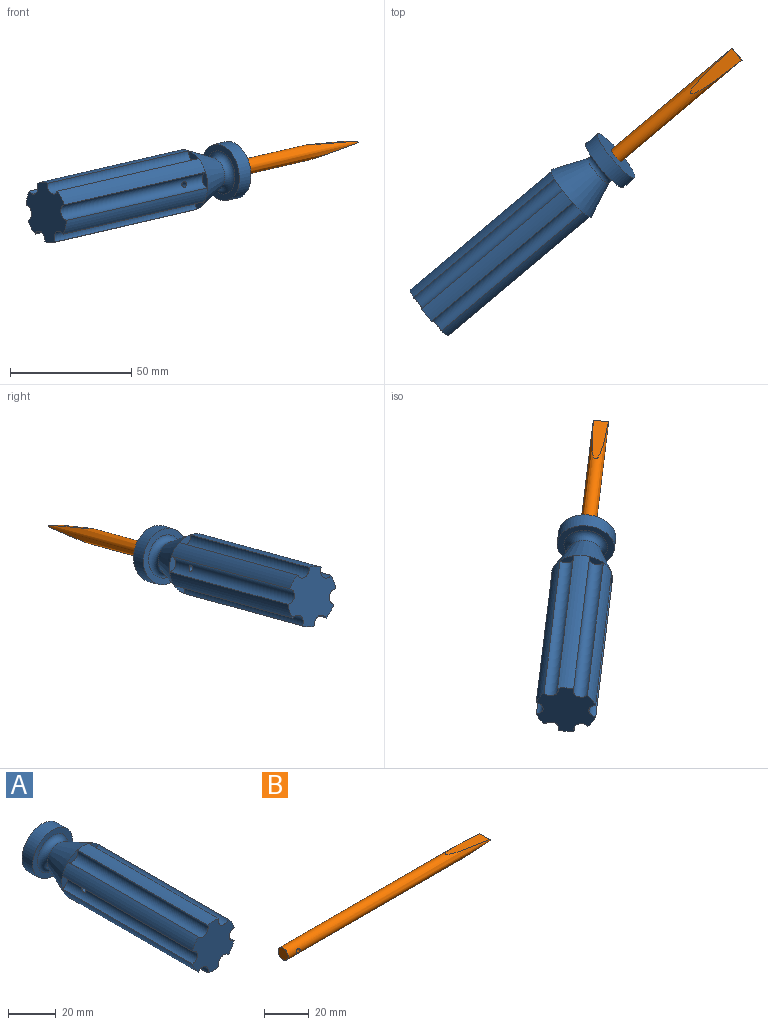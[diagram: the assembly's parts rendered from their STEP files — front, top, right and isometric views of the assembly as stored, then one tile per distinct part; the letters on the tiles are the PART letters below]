
ASSEMBLY  parts=2 mates=1
PART A: 28 faces, bbox 25.4x101.6x25.4 mm
  f0: cylinder r=12.7mm len=77.22mm, axis (0,-1,0), area 516.8mm2, adj f5,f6,f21,f23
  f1: cylinder r=12.7mm len=77.22mm, axis (0,-1,0), area 516.8mm2, adj f5,f6,f19,f21
  f2: cylinder r=12.7mm len=77.22mm, axis (0,-1,0), area 516.8mm2, adj f5,f6,f17,f19
  f3: cylinder r=12.7mm len=77.22mm, axis (0,-1,0), area 516.8mm2, adj f5,f6,f15,f17
  f4: cylinder r=12.7mm len=77.22mm, axis (0,-1,0), area 516.8mm2, adj f5,f6,f13,f15
  f5: plane 25.4x24.55mm, normal (0,-1,0), area 411.9mm2, adj f0,f1,f2,f3,f4,f7,f13,f15
  f6: cone r=12.7mm half-angle=22.3deg, axis (0,-1,0), area 959.6mm2, adj f0,f1,f2,f3,f4,f7,f11,f12
  f7: cylinder r=12.7mm len=77.22mm, axis (0,-1,0), area 516.8mm2, adj f5,f6,f13,f23
  f8: plane 23.71x23.71mm, normal (0,1,0), area 409.9mm2, adj f9,f24
  f9: cylinder r=11.86mm len=23.71mm, axis (0,-1,0), area 473mm2, adj f8,f10
  f10: plane 23.71x23.71mm, normal (0,-1,0), area 183.5mm2, adj f9,f11
  f11: torus R=9.06mm, axis (0,-1,0), area 226.9mm2, adj f6,f10
  f12: plane 6.53x3.25mm, normal (0,-1,0), area 15.8mm2, adj f6,f13
  f13: cylinder r=3.3mm len=77.22mm, axis (0,-1,0), area 721.4mm2, adj f4,f5,f7,f12,f26
  f14: plane 5.89x4.52mm, normal (0,-1,0), area 15.8mm2, adj f6,f15
  f15: cylinder r=3.3mm len=77.22mm, axis (0,-1,0), area 726mm2, adj f3,f4,f5,f14
  f16: plane 5.89x4.52mm, normal (0,-1,0), area 15.8mm2, adj f6,f17
  f17: cylinder r=3.3mm len=77.22mm, axis (0,-1,0), area 726mm2, adj f2,f3,f5,f16
  f18: plane 6.53x3.25mm, normal (0,-1,0), area 15.8mm2, adj f6,f19
  f19: cylinder r=3.3mm len=77.22mm, axis (0,-1,0), area 721.4mm2, adj f1,f2,f5,f18,f27
  f20: plane 5.89x4.52mm, normal (0,-1,0), area 15.8mm2, adj f6,f21
  f21: cylinder r=3.3mm len=77.22mm, axis (0,-1,0), area 726mm2, adj f0,f1,f5,f20
  f22: plane 5.89x4.52mm, normal (0,-1,0), area 15.8mm2, adj f6,f23
  f23: cylinder r=3.3mm len=77.22mm, axis (0,-1,0), area 726mm2, adj f0,f5,f7,f22
  f24: cylinder r=3.17mm len=60.96mm, axis (0,-1,0), area 1207mm2, adj f8,f25,f26,f27
  f25: plane 6.35x6.35mm, normal (0,1,0), area 31.7mm2, adj f24
  f26: cylinder r=1.19mm len=6.74mm, axis (1,0,0), area 48.8mm2, adj f13,f24
  f27: cylinder r=1.19mm len=6.74mm, axis (1,0,0), area 48.8mm2, adj f19,f24
PART B: 6 faces, bbox 127x6.4x6.4 mm
  f0: cylinder r=3.17mm len=127mm, axis (1,0,0), area 2230.3mm2, adj f1,f2,f3,f4,f5
  f1: plane 6.35x0.76mm, normal (1,0,0), area 4.8mm2, adj f0,f3,f4
  f2: plane 6.35x6.35mm, normal (-1,0,0), area 31.7mm2, adj f0
  f3: plane 24.89x6.3mm, normal (0.11,0,-0.99), area 120.3mm2, adj f0,f1
  f4: plane 24.89x6.3mm, normal (0.11,0,0.99), area 120.3mm2, adj f0,f1
  f5: cylinder r=1.19mm len=6.35mm, axis (0,1,0), area 45.9mm2, adj f0
PLACE A rot(axis=(0.18,-0.09,-0.98),50.9deg) t=(-185.99,-118.52,-30.8)mm
PLACE B rot(axis=(0.08,-0.23,0.97),41.2deg) t=(-59.53,-12.4,-1.69)mm
MATE slider B.f0 <-> A.f0  axis (0.75,0.63,0.17) through (-155.33,-92.79,-23.74)mm
